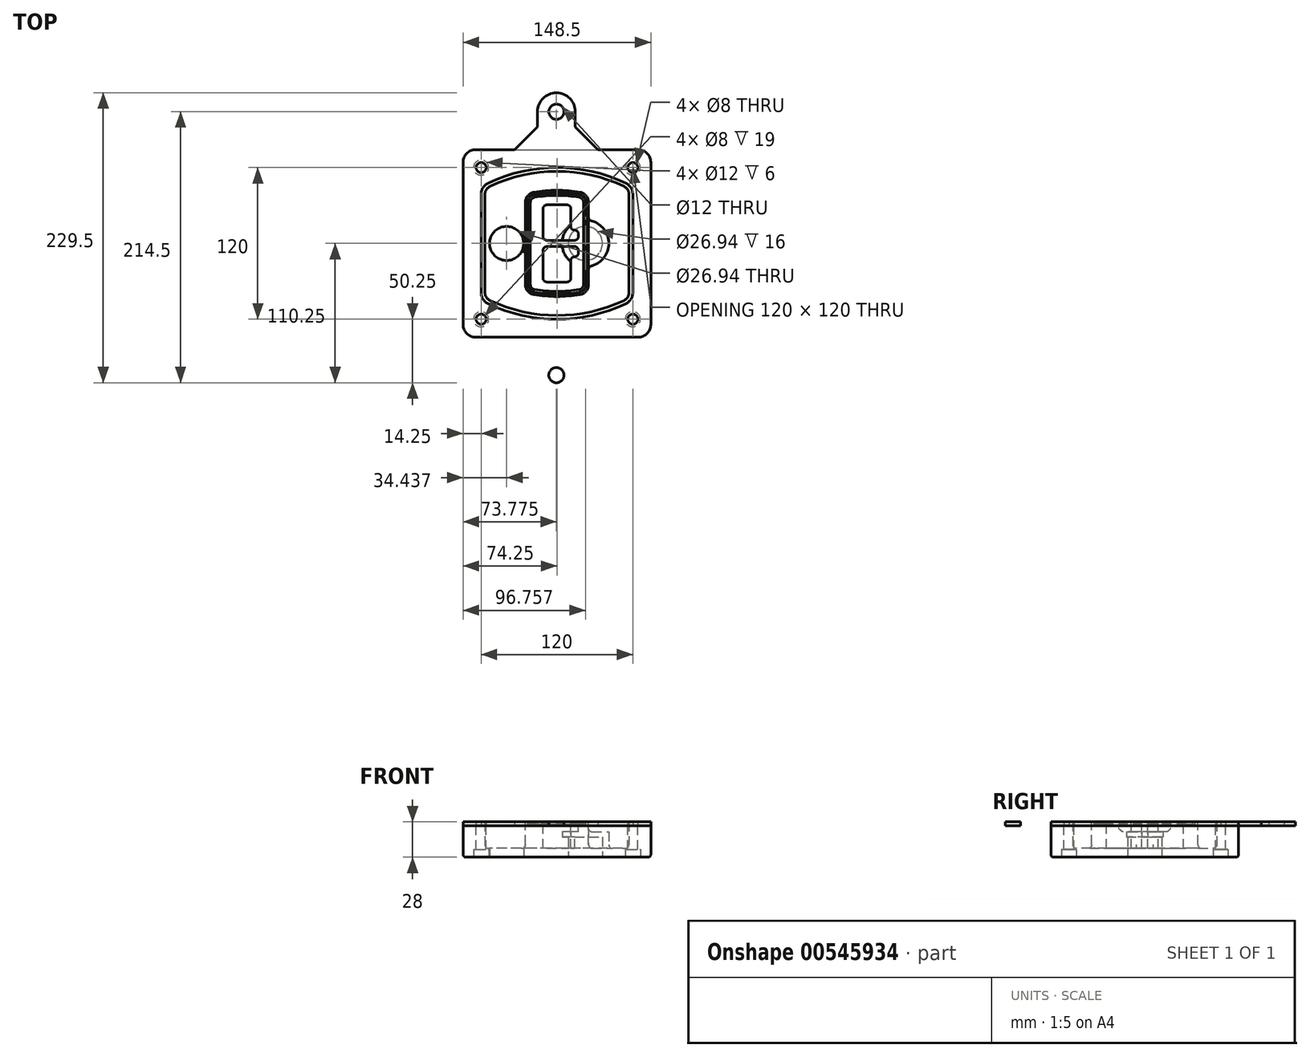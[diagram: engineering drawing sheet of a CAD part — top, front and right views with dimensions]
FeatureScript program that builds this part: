
annotation { "Feature Type Name" : "Feature", "Feature Type Description" : "" }
export const myFeature = defineFeature(function(context is Context, id is Id, definition is map)
    precondition{}
    {
        {
            var Q0;
            Q0=qCreatedBy(makeId("Top.planeOp"),FACE);
            var sketch = newSketch(context, id + "F0", { "sketchPlane" : qUnion([Q0])});
            skPoint(sketch, "E0.rect.middle", {"position": v(0, 0) * mm});
            skLineSegment(sketch, "E1.bottom", {"start": v(-64.25, -74.25) * mm, "end": v(64.25, -74.25) * mm});
            skLineSegment(sketch, "E1.top", {"start": v(-64.25, 74.25) * mm, "end": v(64.25, 74.25) * mm});
            skLineSegment(sketch, "E1.left", {"start": v(-74.25, -64.25) * mm, "end": v(-74.25, 64.25) * mm});
            skLineSegment(sketch, "E1.right", {"start": v(74.25, -64.25) * mm, "end": v(74.25, 64.25) * mm});
            skLineSegment(sketch, "E2", {"start": v(-74.25, 74.25) * mm, "end": v(74.25, -74.25) * mm, "construction": true});
            skLineSegment(sketch, "E3", {"start": v(74.25, 74.25) * mm, "end": v(-74.25, -74.25) * mm, "construction": true});
            skCircle(sketch, "E4", {"center": v(-60, 60) * mm, "radius": 4 * mm});
            skCircle(sketch, "E5", {"center": v(60, 60) * mm, "radius": 4 * mm});
            skCircle(sketch, "E6", {"center": v(60, -60) * mm, "radius": 4 * mm});
            skCircle(sketch, "E7", {"center": v(-60, -60) * mm, "radius": 4 * mm});
            skLineSegment(sketch, "E8", {"start": v(-60, 60) * mm, "end": v(60, 60) * mm, "construction": true});
            skLineSegment(sketch, "E9", {"start": v(60, 60) * mm, "end": v(60, -60) * mm, "construction": true});
            skLineSegment(sketch, "E10", {"start": v(60, -60) * mm, "end": v(-60, -60) * mm, "construction": true});
            skLineSegment(sketch, "E11", {"start": v(-60, -60) * mm, "end": v(-60, 60) * mm, "construction": true});
            skLineSegment(sketch, "E12", {"start": v(-60, 38.83) * mm, "end": v(-60, -38.83) * mm});
            skLineSegment(sketch, "E13", {"start": v(60, 38.83) * mm, "end": v(60, -38.83) * mm});
            skArc(sketch, "E14", {"start": v(54.26, 47.88) * mm, "mid": v(0, 60) * mm, "end": v(-54.26, 47.88) * mm});
            skArc(sketch, "E15", {"start": v(-54.26, -47.88) * mm, "mid": v(0, -60) * mm, "end": v(54.26, -47.88) * mm});
            skLineSegment(sketch, "E16", {"start": v(-60, 0) * mm, "end": v(60, 0) * mm, "construction": true});
            skPoint(sketch, "E17.visualSharp", {"position": v(-60, -45) * mm});
            skArc(sketch, "E17.filletArc", {"start": v(-60, -38.83) * mm, "mid": v(-58.44, -44.2) * mm, "end": v(-54.26, -47.88) * mm});
            skPoint(sketch, "E18.visualSharp", {"position": v(-60, 45) * mm});
            skArc(sketch, "E18.filletArc", {"start": v(-54.26, 47.88) * mm, "mid": v(-58.44, 44.2) * mm, "end": v(-60, 38.83) * mm});
            skPoint(sketch, "E19.visualSharp", {"position": v(60, 45) * mm});
            skArc(sketch, "E19.filletArc", {"start": v(60, 38.83) * mm, "mid": v(58.44, 44.2) * mm, "end": v(54.26, 47.88) * mm});
            skPoint(sketch, "E20.visualSharp", {"position": v(60, -45) * mm});
            skArc(sketch, "E20.filletArc", {"start": v(54.26, -47.88) * mm, "mid": v(58.44, -44.2) * mm, "end": v(60, -38.83) * mm});
            skPoint(sketch, "E21.visualSharp", {"position": v(-74.25, 74.25) * mm});
            skArc(sketch, "E21.filletArc", {"start": v(-64.25, 74.25) * mm, "mid": v(-71.32, 71.32) * mm, "end": v(-74.25, 64.25) * mm});
            skPoint(sketch, "E22.visualSharp", {"position": v(74.25, 74.25) * mm});
            skArc(sketch, "E22.filletArc", {"start": v(74.25, 64.25) * mm, "mid": v(71.32, 71.32) * mm, "end": v(64.25, 74.25) * mm});
            skPoint(sketch, "E23.visualSharp", {"position": v(74.25, -74.25) * mm});
            skArc(sketch, "E23.filletArc", {"start": v(64.25, -74.25) * mm, "mid": v(71.32, -71.32) * mm, "end": v(74.25, -64.25) * mm});
            skPoint(sketch, "E24.visualSharp", {"position": v(-74.25, -74.25) * mm});
            skArc(sketch, "E24.filletArc", {"start": v(-74.25, -64.25) * mm, "mid": v(-71.32, -71.32) * mm, "end": v(-64.25, -74.25) * mm});
            skArc(sketch, "E25.0", {"start": v(57, 38.83) * mm, "mid": v(55.9, 42.58) * mm, "end": v(52.98, 45.17) * mm});
            skLineSegment(sketch, "E25.1", {"start": v(57, 38.83) * mm, "end": v(57, -38.83) * mm});
            skArc(sketch, "E25.2", {"start": v(52.98, -45.17) * mm, "mid": v(55.9, -42.58) * mm, "end": v(57, -38.83) * mm});
            skArc(sketch, "E25.3", {"start": v(-52.98, -45.17) * mm, "mid": v(0, -57) * mm, "end": v(52.98, -45.17) * mm});
            skArc(sketch, "E25.4", {"start": v(-57, -38.83) * mm, "mid": v(-55.9, -42.58) * mm, "end": v(-52.98, -45.17) * mm});
            skArc(sketch, "E25.5", {"start": v(52.98, 45.17) * mm, "mid": v(0, 57) * mm, "end": v(-52.98, 45.17) * mm});
            skLineSegment(sketch, "E25.6", {"start": v(-57, 38.83) * mm, "end": v(-57, -38.83) * mm});
            skArc(sketch, "E25.7", {"start": v(-52.98, 45.17) * mm, "mid": v(-55.9, 42.58) * mm, "end": v(-57, 38.83) * mm});
            skArc(sketch, "E26.0", {"start": v(-55.96, 51.5) * mm, "mid": v(-61.82, 46.33) * mm, "end": v(-64, 38.83) * mm});
            skArc(sketch, "E26.1", {"start": v(55.96, 51.5) * mm, "mid": v(0, 64) * mm, "end": v(-55.96, 51.5) * mm});
            skArc(sketch, "E26.2", {"start": v(64, 38.83) * mm, "mid": v(61.82, 46.33) * mm, "end": v(55.96, 51.5) * mm});
            skLineSegment(sketch, "E26.3", {"start": v(64, 38.83) * mm, "end": v(64, -38.83) * mm});
            skArc(sketch, "E26.4", {"start": v(55.96, -51.5) * mm, "mid": v(61.82, -46.33) * mm, "end": v(64, -38.83) * mm});
            skLineSegment(sketch, "E26.5", {"start": v(-64, 38.83) * mm, "end": v(-64, -38.83) * mm});
            skArc(sketch, "E26.6", {"start": v(-55.96, -51.5) * mm, "mid": v(0, -64) * mm, "end": v(55.96, -51.5) * mm});
            skArc(sketch, "E26.7", {"start": v(-64, -38.83) * mm, "mid": v(-61.82, -46.33) * mm, "end": v(-55.96, -51.5) * mm});
            skSolve(sketch);
        }
        {
            var Q0;
            Q0=makeQuery(id+"F0.imprint","IMPRINT",FACE,{"disambiguationData":[TD([[makeQuery(id+"F0.imprint","IMPRINT",EDGE,{"derivedFrom":sQuery(id+"F0.wireOp",EDGE,"E1.bottom")}),1.0]])]});
            var Q1;
            Q1=makeQuery(id+"F0.imprint","IMPRINT",FACE,{"disambiguationData":[TD([[makeQuery(id+"F0.imprint","IMPRINT",EDGE,{"derivedFrom":sQuery(id+"F0.wireOp",EDGE,"E12")}),1.0]])]});
            var Q2;
            Q2=makeQuery(id+"F0.imprint","IMPRINT",FACE,{"disambiguationData":[TD([[makeQuery(id+"F0.imprint","IMPRINT",EDGE,{"derivedFrom":sQuery(id+"F0.wireOp",EDGE,"E25.0")}),1.0]])]});
            var Q3;
            Q3=makeQuery(id+"F0.imprint","IMPRINT",FACE,{"disambiguationData":[TD([[makeQuery(id+"F0.imprint","IMPRINT",EDGE,{"derivedFrom":sQuery(id+"F0.wireOp",EDGE,"E12")}),-1.0]])]});
            extrude(context, id + "F1", {"entities" : qUnion([Q0, Q1, Q2, Q3]), "oppositeDirection" : true, "depth" : 25 * mm});
        }
        {
            var Q0;
            Q0=makeQuery(id+"F0.imprint","IMPRINT",FACE,{"disambiguationData":[TD([[makeQuery(id+"F0.imprint","IMPRINT",EDGE,{"derivedFrom":sQuery(id+"F0.wireOp",EDGE,"E12")}),1.0]])]});
            extrude(context, id + "F2", {"entities" : qUnion([Q0]), "operationType" : NewBodyOperationType.ADD, "depth" : 3 * mm});
        }
        {
            var Q0;
            Q0=makeQuery(id+"F0.imprint","IMPRINT",FACE,{"disambiguationData":[TD([[makeQuery(id+"F0.imprint","IMPRINT",EDGE,{"derivedFrom":sQuery(id+"F0.wireOp",EDGE,"E25.0")}),1.0]])]});
            extrude(context, id + "F3", {"entities" : qUnion([Q0]), "operationType" : NewBodyOperationType.REMOVE, "oppositeDirection" : true, "depth" : 18 * mm});
        }
        {
            var Q0;
            Q0=makeQuery(id+"F2.opExtrude","CAP_FACE",FACE,{"disambiguationData":[OSD([sQuery(id+"F0.wireOp",EDGE,"E12"),sQuery(id+"F0.wireOp",EDGE,"E13"),sQuery(id+"F0.wireOp",EDGE,"E14"),sQuery(id+"F0.wireOp",EDGE,"E15"),sQuery(id+"F0.wireOp",EDGE,"E17.filletArc"),sQuery(id+"F0.wireOp",EDGE,"E18.filletArc"),sQuery(id+"F0.wireOp",EDGE,"E19.filletArc"),sQuery(id+"F0.wireOp",EDGE,"E20.filletArc"),sQuery(id+"F0.wireOp",EDGE,"E25.0"),sQuery(id+"F0.wireOp",EDGE,"E25.1"),sQuery(id+"F0.wireOp",EDGE,"E25.2"),sQuery(id+"F0.wireOp",EDGE,"E25.3"),sQuery(id+"F0.wireOp",EDGE,"E25.4"),sQuery(id+"F0.wireOp",EDGE,"E25.5"),sQuery(id+"F0.wireOp",EDGE,"E25.6"),sQuery(id+"F0.wireOp",EDGE,"E25.7")])],"isStart":false});
            var sketch = newSketch(context, id + "F4", { "sketchPlane" : qUnion([Q0])});
            skArc(sketch, "E27.0", {"start": v(-18.34, -40.45) * mm, "mid": v(0, -42) * mm, "end": v(18.34, -40.45) * mm});
            skArc(sketch, "E28.0", {"start": v(18.34, 40.45) * mm, "mid": v(0, 42) * mm, "end": v(-18.34, 40.45) * mm});
            skLineSegment(sketch, "E29", {"start": v(-25, 32.57) * mm, "end": v(-25, -32.57) * mm});
            skLineSegment(sketch, "E30", {"start": v(25, 32.57) * mm, "end": v(25, -32.57) * mm});
            skLineSegment(sketch, "E31", {"start": v(-25, 39.1) * mm, "end": v(25, 39.1) * mm, "construction": true});
            skLineSegment(sketch, "E32", {"start": v(-25, -39.1) * mm, "end": v(25, -39.1) * mm, "construction": true});
            skPoint(sketch, "E33.visualSharp", {"position": v(-25, 39.1) * mm});
            skArc(sketch, "E33.filletArc", {"start": v(-18.34, 40.45) * mm, "mid": v(-23.11, 37.73) * mm, "end": v(-25, 32.57) * mm});
            skPoint(sketch, "E34.visualSharp", {"position": v(25, 39.1) * mm});
            skArc(sketch, "E34.filletArc", {"start": v(25, 32.57) * mm, "mid": v(23.11, 37.73) * mm, "end": v(18.34, 40.45) * mm});
            skPoint(sketch, "E35.visualSharp", {"position": v(25, -39.1) * mm});
            skArc(sketch, "E35.filletArc", {"start": v(18.34, -40.45) * mm, "mid": v(23.11, -37.73) * mm, "end": v(25, -32.57) * mm});
            skPoint(sketch, "E36.visualSharp", {"position": v(-25, -39.1) * mm});
            skArc(sketch, "E36.filletArc", {"start": v(-25, -32.57) * mm, "mid": v(-23.11, -37.73) * mm, "end": v(-18.34, -40.45) * mm});
            skArc(sketch, "E37.0", {"start": v(52.98, 45.17) * mm, "mid": v(0, 57) * mm, "end": v(-52.98, 45.17) * mm});
            skArc(sketch, "E37.1", {"start": v(-52.98, 45.17) * mm, "mid": v(-55.9, 42.58) * mm, "end": v(-57, 38.83) * mm});
            skLineSegment(sketch, "E37.2", {"start": v(-57, 38.83) * mm, "end": v(-57, -38.83) * mm});
            skArc(sketch, "E37.3", {"start": v(-57, -38.83) * mm, "mid": v(-55.9, -42.58) * mm, "end": v(-52.98, -45.17) * mm});
            skArc(sketch, "E37.4", {"start": v(-52.98, -45.17) * mm, "mid": v(0, -57) * mm, "end": v(52.98, -45.17) * mm});
            skArc(sketch, "E37.5", {"start": v(52.98, -45.17) * mm, "mid": v(55.9, -42.58) * mm, "end": v(57, -38.83) * mm});
            skLineSegment(sketch, "E37.6", {"start": v(57, 38.83) * mm, "end": v(57, -38.83) * mm});
            skArc(sketch, "E37.7", {"start": v(57, 38.83) * mm, "mid": v(55.9, 42.58) * mm, "end": v(52.98, 45.17) * mm});
            skLineSegment(sketch, "E38.0", {"start": v(23, 32.57) * mm, "end": v(23, -32.57) * mm});
            skArc(sketch, "E38.1", {"start": v(18, -38.48) * mm, "mid": v(21.58, -36.44) * mm, "end": v(23, -32.57) * mm});
            skArc(sketch, "E38.2", {"start": v(-18, -38.48) * mm, "mid": v(0, -40) * mm, "end": v(18, -38.48) * mm});
            skArc(sketch, "E38.3", {"start": v(-23, -32.57) * mm, "mid": v(-21.58, -36.44) * mm, "end": v(-18, -38.48) * mm});
            skLineSegment(sketch, "E38.4", {"start": v(-23, 32.57) * mm, "end": v(-23, -32.57) * mm});
            skArc(sketch, "E38.5", {"start": v(23, 32.57) * mm, "mid": v(21.58, 36.44) * mm, "end": v(18, 38.48) * mm});
            skArc(sketch, "E38.6", {"start": v(-18, 38.48) * mm, "mid": v(-21.58, 36.44) * mm, "end": v(-23, 32.57) * mm});
            skArc(sketch, "E38.7", {"start": v(18, 38.48) * mm, "mid": v(0, 40) * mm, "end": v(-18, 38.48) * mm});
            skArc(sketch, "E39.0", {"start": v(21, 32.57) * mm, "mid": v(20.06, 35.15) * mm, "end": v(17.67, 36.5) * mm});
            skLineSegment(sketch, "E39.1", {"start": v(21, 32.57) * mm, "end": v(21, -32.57) * mm});
            skArc(sketch, "E39.2", {"start": v(17.67, -36.5) * mm, "mid": v(20.06, -35.15) * mm, "end": v(21, -32.57) * mm});
            skArc(sketch, "E39.3", {"start": v(-17.67, -36.5) * mm, "mid": v(0, -38) * mm, "end": v(17.67, -36.5) * mm});
            skArc(sketch, "E39.4", {"start": v(-21, -32.57) * mm, "mid": v(-20.06, -35.15) * mm, "end": v(-17.67, -36.5) * mm});
            skArc(sketch, "E39.5", {"start": v(17.67, 36.5) * mm, "mid": v(0, 38) * mm, "end": v(-17.67, 36.5) * mm});
            skLineSegment(sketch, "E39.6", {"start": v(-21, 32.57) * mm, "end": v(-21, -32.57) * mm});
            skArc(sketch, "E39.7", {"start": v(-17.67, 36.5) * mm, "mid": v(-20.06, 35.15) * mm, "end": v(-21, 32.57) * mm});
            skLineSegment(sketch, "E40", {"start": v(-25, 0) * mm, "end": v(25, 0) * mm, "construction": true});
            skLineSegment(sketch, "E41", {"start": v(-11, 5.5) * mm, "end": v(-11, 27.5) * mm});
            skLineSegment(sketch, "E42", {"start": v(-8, 30.5) * mm, "end": v(8, 30.5) * mm});
            skLineSegment(sketch, "E43", {"start": v(11, 27.5) * mm, "end": v(11, 13.5) * mm});
            skLineSegment(sketch, "E44", {"start": v(14, 10.5) * mm, "end": v(14, 10.5) * mm});
            skLineSegment(sketch, "E45", {"start": v(17, 7.5) * mm, "end": v(17, 5.5) * mm});
            skLineSegment(sketch, "E46", {"start": v(14, 2.5) * mm, "end": v(-8, 2.5) * mm});
            skPoint(sketch, "E47.visualSharp", {"position": v(-11, 30.5) * mm});
            skArc(sketch, "E47.filletArc", {"start": v(-8, 30.5) * mm, "mid": v(-10.12, 29.62) * mm, "end": v(-11, 27.5) * mm});
            skPoint(sketch, "E48.visualSharp", {"position": v(11, 30.5) * mm});
            skArc(sketch, "E48.filletArc", {"start": v(11, 27.5) * mm, "mid": v(10.12, 29.62) * mm, "end": v(8, 30.5) * mm});
            skPoint(sketch, "E49.visualSharp", {"position": v(11, 10.5) * mm});
            skArc(sketch, "E49.filletArc", {"start": v(11, 13.5) * mm, "mid": v(11.88, 11.38) * mm, "end": v(14, 10.5) * mm});
            skPoint(sketch, "E50.visualSharp", {"position": v(17, 10.5) * mm});
            skArc(sketch, "E50.filletArc", {"start": v(17, 7.5) * mm, "mid": v(16.12, 9.62) * mm, "end": v(14, 10.5) * mm});
            skPoint(sketch, "E51.visualSharp", {"position": v(17, 2.5) * mm});
            skArc(sketch, "E51.filletArc", {"start": v(14, 2.5) * mm, "mid": v(16.12, 3.38) * mm, "end": v(17, 5.5) * mm});
            skPoint(sketch, "E52.visualSharp", {"position": v(-11, 2.5) * mm});
            skArc(sketch, "E52.filletArc", {"start": v(-11, 5.5) * mm, "mid": v(-10.12, 3.38) * mm, "end": v(-8, 2.5) * mm});
            skLineSegment(sketch, "E53.0.MirrorCS", {"start": v(14, -2.5) * mm, "end": v(-8, -2.5) * mm});
            skArc(sketch, "E54.0.MirrorCS", {"start": v(-11, -5.5) * mm, "mid": v(-10.12, -3.38) * mm, "end": v(-8, -2.5) * mm});
            skLineSegment(sketch, "E55.0.MirrorCS", {"start": v(-11, -5.5) * mm, "end": v(-11, -27.5) * mm});
            skArc(sketch, "E56.0.MirrorCS", {"start": v(-8, -30.5) * mm, "mid": v(-10.12, -29.62) * mm, "end": v(-11, -27.5) * mm});
            skLineSegment(sketch, "E57.0.MirrorCS", {"start": v(-8, -30.5) * mm, "end": v(8, -30.5) * mm});
            skArc(sketch, "E58.0.MirrorCS", {"start": v(11, -27.5) * mm, "mid": v(10.12, -29.62) * mm, "end": v(8, -30.5) * mm});
            skLineSegment(sketch, "E59.0.MirrorCS", {"start": v(11, -27.5) * mm, "end": v(11, -13.5) * mm});
            skArc(sketch, "E60.0.MirrorCS", {"start": v(11, -13.5) * mm, "mid": v(11.88, -11.38) * mm, "end": v(14, -10.5) * mm});
            skArc(sketch, "E61.0.MirrorCS", {"start": v(17, -7.5) * mm, "mid": v(16.12, -9.62) * mm, "end": v(14, -10.5) * mm});
            skLineSegment(sketch, "E62.0.MirrorCS", {"start": v(17, -7.5) * mm, "end": v(17, -5.5) * mm});
            skArc(sketch, "E63.0.MirrorCS", {"start": v(14, -2.5) * mm, "mid": v(16.12, -3.38) * mm, "end": v(17, -5.5) * mm});
            skSolve(sketch);
        }
        {
            var Q0;
            Q0=makeQuery(id+"F4.imprint","IMPRINT",FACE,{"disambiguationData":[TD([[makeQuery(id+"F4.imprint","IMPRINT",EDGE,{"derivedFrom":sQuery(id+"F4.wireOp",EDGE,"E27.0")}),1.0]])]});
            var Q1;
            Q1=makeQuery(id+"F4.imprint","IMPRINT",FACE,{"disambiguationData":[TD([[makeQuery(id+"F4.imprint","IMPRINT",EDGE,{"derivedFrom":sQuery(id+"F4.wireOp",EDGE,"E38.0")}),-1.0]])]});
            var Q2;
            Q2=makeQuery(id+"F4.imprint","IMPRINT",FACE,{"disambiguationData":[TD([[makeQuery(id+"F4.imprint","IMPRINT",EDGE,{"derivedFrom":sQuery(id+"F4.wireOp",EDGE,"E39.0")}),1.0]])]});
            extrude(context, id + "F5", {"entities" : qUnion([Q0, Q1, Q2]), "operationType" : NewBodyOperationType.ADD, "endBound" : BoundingType.UP_TO_NEXT, "oppositeDirection" : true, "depth" : 25 * mm});
        }
        {
            var Q0;
            Q0=makeQuery(id+"F4.imprint","IMPRINT",FACE,{"disambiguationData":[TD([[makeQuery(id+"F4.imprint","IMPRINT",EDGE,{"derivedFrom":sQuery(id+"F4.wireOp",EDGE,"E38.0")}),-1.0]])]});
            extrude(context, id + "F6", {"entities" : qUnion([Q0]), "operationType" : NewBodyOperationType.REMOVE, "oppositeDirection" : true, "depth" : 2 * mm});
        }
        {
            var Q0;
            Q0=makeQuery(id+"F1.opExtrude","CAP_FACE",FACE,{"disambiguationData":[OSD([sQuery(id+"F0.wireOp",EDGE,"E1.bottom"),sQuery(id+"F0.wireOp",EDGE,"E1.top"),sQuery(id+"F0.wireOp",EDGE,"E1.left"),sQuery(id+"F0.wireOp",EDGE,"E1.right"),sQuery(id+"F0.wireOp",EDGE,"E4"),sQuery(id+"F0.wireOp",EDGE,"E5"),sQuery(id+"F0.wireOp",EDGE,"E6"),sQuery(id+"F0.wireOp",EDGE,"E7"),sQuery(id+"F0.wireOp",EDGE,"E21.filletArc"),sQuery(id+"F0.wireOp",EDGE,"E22.filletArc"),sQuery(id+"F0.wireOp",EDGE,"E23.filletArc"),sQuery(id+"F0.wireOp",EDGE,"E24.filletArc")])],"isStart":false});
            var sketch = newSketch(context, id + "F7", { "sketchPlane" : qUnion([Q0])});
            skCircle(sketch, "E64", {"center": v(22.5, 0) * mm, "radius": 13.47 * mm});
            skCircle(sketch, "E65", {"center": v(-39.81, 0) * mm, "radius": 13.47 * mm});
            skLineSegment(sketch, "E66", {"start": v(74.25, 0) * mm, "end": v(-74.25, 0) * mm});
            skCircle(sketch, "E67", {"center": v(22.5, 0) * mm, "radius": 18.47 * mm});
            skCircle(sketch, "E68", {"center": v(60, -60) * mm, "radius": 6 * mm});
            skCircle(sketch, "E69", {"center": v(-60, -60) * mm, "radius": 6 * mm});
            skCircle(sketch, "E70", {"center": v(-60, 60) * mm, "radius": 6 * mm});
            skCircle(sketch, "E71", {"center": v(60, 60) * mm, "radius": 6 * mm});
            skSolve(sketch);
        }
        {
            var Q0;
            {var subQ1=sQuery(id+"F7.wireOp",EDGE,"E66");var subQ4=sQuery(id+"F7.wireOp",EDGE,"E64");var subQ6=makeQuery(id+"F7.imprint","INTERSECT",VERTEX,{"disambiguationData":[OD(0.0)],"derivedFrom":[subQ4,subQ1]});Q0=makeQuery(id+"F7.imprint","IMPRINT",FACE,{"disambiguationData":[TD([[makeQuery(id+"F7.imprint","IMPRINT",EDGE,{"disambiguationData":[TD([[subQ6,-1.0]])],"derivedFrom":subQ4}),-1.0]])]});}
            var Q1;
            {var subQ0=sQuery(id+"F7.wireOp",EDGE,"E66");var subQ1=sQuery(id+"F7.wireOp",EDGE,"E64");var subQ3=makeQuery(id+"F7.imprint","INTERSECT",VERTEX,{"disambiguationData":[OD(0.0)],"derivedFrom":[subQ1,subQ0]});Q1=makeQuery(id+"F7.imprint","IMPRINT",FACE,{"disambiguationData":[TD([[makeQuery(id+"F7.imprint","IMPRINT",EDGE,{"disambiguationData":[TD([[subQ3,-1.0]])],"derivedFrom":subQ1}),1.0]])]});}
            var Q2;
            {var subQ0=sQuery(id+"F7.wireOp",EDGE,"E66");var subQ1=sQuery(id+"F7.wireOp",EDGE,"E64");var subQ3=makeQuery(id+"F7.imprint","INTERSECT",VERTEX,{"disambiguationData":[OD(0.0)],"derivedFrom":[subQ1,subQ0]});Q2=makeQuery(id+"F7.imprint","IMPRINT",FACE,{"disambiguationData":[TD([[makeQuery(id+"F7.imprint","IMPRINT",EDGE,{"disambiguationData":[TD([[subQ3,1.0]])],"derivedFrom":subQ1}),1.0]])]});}
            var Q3;
            {var subQ1=sQuery(id+"F7.wireOp",EDGE,"E66");var subQ4=sQuery(id+"F7.wireOp",EDGE,"E64");var subQ6=makeQuery(id+"F7.imprint","INTERSECT",VERTEX,{"disambiguationData":[OD(0.0)],"derivedFrom":[subQ4,subQ1]});Q3=makeQuery(id+"F7.imprint","IMPRINT",FACE,{"disambiguationData":[TD([[makeQuery(id+"F7.imprint","IMPRINT",EDGE,{"disambiguationData":[TD([[subQ6,1.0]])],"derivedFrom":subQ4}),-1.0]])]});}
            extrude(context, id + "F8", {"entities" : qUnion([Q0, Q1, Q2, Q3]), "operationType" : NewBodyOperationType.ADD, "oppositeDirection" : true, "depth" : 20 * mm});
        }
        {
            var Q0;
            {var subQ0=sQuery(id+"F7.wireOp",EDGE,"E66");var subQ1=sQuery(id+"F7.wireOp",EDGE,"E64");var subQ3=makeQuery(id+"F7.imprint","INTERSECT",VERTEX,{"disambiguationData":[OD(0.0)],"derivedFrom":[subQ1,subQ0]});Q0=makeQuery(id+"F7.imprint","IMPRINT",FACE,{"disambiguationData":[TD([[makeQuery(id+"F7.imprint","IMPRINT",EDGE,{"disambiguationData":[TD([[subQ3,-1.0]])],"derivedFrom":subQ1}),1.0]])]});}
            var Q1;
            {var subQ0=sQuery(id+"F7.wireOp",EDGE,"E66");var subQ1=sQuery(id+"F7.wireOp",EDGE,"E64");var subQ3=makeQuery(id+"F7.imprint","INTERSECT",VERTEX,{"disambiguationData":[OD(0.0)],"derivedFrom":[subQ1,subQ0]});Q1=makeQuery(id+"F7.imprint","IMPRINT",FACE,{"disambiguationData":[TD([[makeQuery(id+"F7.imprint","IMPRINT",EDGE,{"disambiguationData":[TD([[subQ3,1.0]])],"derivedFrom":subQ1}),1.0]])]});}
            extrude(context, id + "F9", {"entities" : qUnion([Q0, Q1]), "operationType" : NewBodyOperationType.REMOVE, "oppositeDirection" : true, "depth" : 16 * mm});
        }
        {
            var Q0;
            {var subQ0=sQuery(id+"F7.wireOp",EDGE,"E66");var subQ1=sQuery(id+"F7.wireOp",EDGE,"E65");var subQ3=makeQuery(id+"F7.imprint","INTERSECT",VERTEX,{"disambiguationData":[OD(0.0)],"derivedFrom":[subQ1,subQ0]});Q0=makeQuery(id+"F7.imprint","IMPRINT",FACE,{"disambiguationData":[TD([[makeQuery(id+"F7.imprint","IMPRINT",EDGE,{"disambiguationData":[TD([[subQ3,-1.0]])],"derivedFrom":subQ1}),1.0]])]});}
            var Q1;
            {var subQ0=sQuery(id+"F7.wireOp",EDGE,"E66");var subQ1=sQuery(id+"F7.wireOp",EDGE,"E65");var subQ3=makeQuery(id+"F7.imprint","INTERSECT",VERTEX,{"disambiguationData":[OD(0.0)],"derivedFrom":[subQ1,subQ0]});Q1=makeQuery(id+"F7.imprint","IMPRINT",FACE,{"disambiguationData":[TD([[makeQuery(id+"F7.imprint","IMPRINT",EDGE,{"disambiguationData":[TD([[subQ3,1.0]])],"derivedFrom":subQ1}),1.0]])]});}
            extrude(context, id + "F10", {"entities" : qUnion([Q0, Q1]), "operationType" : NewBodyOperationType.REMOVE, "oppositeDirection" : true, "depth" : 25 * mm});
        }
        {
            var Q0;
            Q0=makeQuery(id+"F7.imprint","IMPRINT",FACE,{"disambiguationData":[TD([[makeQuery(id+"F7.imprint","IMPRINT",EDGE,{"derivedFrom":sQuery(id+"F7.wireOp",EDGE,"E68")}),1.0]])]});
            var Q1;
            Q1=makeQuery(id+"F7.imprint","IMPRINT",FACE,{"disambiguationData":[TD([[makeQuery(id+"F7.imprint","IMPRINT",EDGE,{"derivedFrom":makeQuery(id+"F1.opExtrude","CAP_EDGE",EDGE,{"disambiguationData":[OSD([sQuery(id+"F0.wireOp",EDGE,"E5")])],"isStart":false})}),-1.0]])]});
            var Q2;
            Q2=makeQuery(id+"F7.imprint","IMPRINT",FACE,{"disambiguationData":[TD([[makeQuery(id+"F7.imprint","IMPRINT",EDGE,{"derivedFrom":sQuery(id+"F7.wireOp",EDGE,"E69")}),1.0]])]});
            var Q3;
            Q3=makeQuery(id+"F7.imprint","IMPRINT",FACE,{"disambiguationData":[TD([[makeQuery(id+"F7.imprint","IMPRINT",EDGE,{"derivedFrom":makeQuery(id+"F1.opExtrude","CAP_EDGE",EDGE,{"disambiguationData":[OSD([sQuery(id+"F0.wireOp",EDGE,"E4")])],"isStart":false})}),-1.0]])]});
            var Q4;
            Q4=makeQuery(id+"F7.imprint","IMPRINT",FACE,{"disambiguationData":[TD([[makeQuery(id+"F7.imprint","IMPRINT",EDGE,{"derivedFrom":sQuery(id+"F7.wireOp",EDGE,"E70")}),1.0]])]});
            var Q5;
            Q5=makeQuery(id+"F7.imprint","IMPRINT",FACE,{"disambiguationData":[TD([[makeQuery(id+"F7.imprint","IMPRINT",EDGE,{"derivedFrom":makeQuery(id+"F1.opExtrude","CAP_EDGE",EDGE,{"disambiguationData":[OSD([sQuery(id+"F0.wireOp",EDGE,"E7")])],"isStart":false})}),-1.0]])]});
            var Q6;
            Q6=makeQuery(id+"F7.imprint","IMPRINT",FACE,{"disambiguationData":[TD([[makeQuery(id+"F7.imprint","IMPRINT",EDGE,{"derivedFrom":sQuery(id+"F7.wireOp",EDGE,"E71")}),1.0]])]});
            var Q7;
            Q7=makeQuery(id+"F7.imprint","IMPRINT",FACE,{"disambiguationData":[TD([[makeQuery(id+"F7.imprint","IMPRINT",EDGE,{"derivedFrom":makeQuery(id+"F1.opExtrude","CAP_EDGE",EDGE,{"disambiguationData":[OSD([sQuery(id+"F0.wireOp",EDGE,"E6")])],"isStart":false})}),-1.0]])]});
            extrude(context, id + "F11", {"entities" : qUnion([Q0, Q1, Q2, Q3, Q4, Q5, Q6, Q7]), "operationType" : NewBodyOperationType.REMOVE, "oppositeDirection" : true, "depth" : 6 * mm});
        }
        {
            var Q0;
            Q0=makeQuery(id+"F9.boolean.opBoolean","COPY",FACE,{"derivedFrom":makeQuery(id+"F9.opExtrude","CAP_FACE",FACE,{"disambiguationData":[OSD([sQuery(id+"F7.wireOp",EDGE,"E64")])],"isStart":false})});
            var sketch = newSketch(context, id + "F12", { "sketchPlane" : qUnion([Q0])});
            skArc(sketch, "E72.0", {"start": v(11, 14.45) * mm, "mid": v(6.45, 9.13) * mm, "end": v(4.2, 2.5) * mm});
            skArc(sketch, "E72.1", {"start": v(4.2, -2.5) * mm, "mid": v(6.45, -9.13) * mm, "end": v(11, -14.45) * mm});
            skLineSegment(sketch, "E73", {"start": v(4.2, -2.5) * mm, "end": v(14, -2.5) * mm});
            skLineSegment(sketch, "E74.0", {"start": v(14, 2.5) * mm, "end": v(4.2, 2.5) * mm});
            skArc(sketch, "E74.1", {"start": v(14, 2.5) * mm, "mid": v(16.12, 3.38) * mm, "end": v(17, 5.5) * mm});
            skLineSegment(sketch, "E74.2", {"start": v(17, 7.5) * mm, "end": v(17, 5.5) * mm});
            skArc(sketch, "E74.3", {"start": v(17, 7.5) * mm, "mid": v(16.12, 9.62) * mm, "end": v(14, 10.5) * mm});
            skArc(sketch, "E74.4", {"start": v(11, 13.5) * mm, "mid": v(11.88, 11.38) * mm, "end": v(14, 10.5) * mm});
            skLineSegment(sketch, "E74.5", {"start": v(11, 14.45) * mm, "end": v(11, 13.5) * mm});
            skLineSegment(sketch, "E74.7", {"start": v(14, -2.5) * mm, "end": v(4.2, -2.5) * mm});
            skArc(sketch, "E74.8", {"start": v(14, -2.5) * mm, "mid": v(16.12, -3.38) * mm, "end": v(17, -5.5) * mm});
            skLineSegment(sketch, "E74.9", {"start": v(17, -7.5) * mm, "end": v(17, -5.5) * mm});
            skArc(sketch, "E74.10", {"start": v(17, -7.5) * mm, "mid": v(16.12, -9.62) * mm, "end": v(14, -10.5) * mm});
            skArc(sketch, "E74.11", {"start": v(11, -13.5) * mm, "mid": v(11.88, -11.38) * mm, "end": v(14, -10.5) * mm});
            skLineSegment(sketch, "E74.12", {"start": v(11, -14.45) * mm, "end": v(11, -13.5) * mm});
            skPoint(sketch, "E75.orphan", {"position": v(11, -27.5) * mm});
            skPoint(sketch, "E76.orphan", {"position": v(-8, -2.5) * mm});
            skPoint(sketch, "E77.orphan", {"position": v(-8, 2.5) * mm});
            skPoint(sketch, "E78.orphan", {"position": v(11, 27.5) * mm});
            skSolve(sketch);
        }
        {
            var Q0;
            {var subQ7=sQuery(id+"F12.wireOp",EDGE,"E72.0");var subQ14=sQuery(id+"F12.wireOp",EDGE,"E72.1");var subQ16=sQuery(id+"F12.wireOp",EDGE,"E74.1");var subQ18=sQuery(id+"F12.wireOp",EDGE,"E74.8");Q0=qUnion([makeQuery(id+"F12.imprint","IMPRINT",FACE,{"disambiguationData":[TD([[makeQuery(id+"F12.imprint","IMPRINT",EDGE,{"derivedFrom":subQ7}),1.0]])]}),makeQuery(id+"F12.imprint","IMPRINT",FACE,{"disambiguationData":[TD([[makeQuery(id+"F12.imprint","IMPRINT",EDGE,{"derivedFrom":subQ14}),1.0]])]}),makeQuery(id+"F12.imprint","IMPRINT",FACE,{"disambiguationData":[TD([[makeQuery(id+"F12.imprint","IMPRINT",EDGE,{"derivedFrom":subQ16}),1.0]])]}),makeQuery(id+"F12.imprint","IMPRINT",FACE,{"disambiguationData":[TD([[makeQuery(id+"F12.imprint","IMPRINT",EDGE,{"derivedFrom":subQ18}),-1.0]])]})]);}
            var Q1;
            Q1=makeQuery(id+"F5.boolean.opBoolean","SPLIT",FACE,{"disambiguationData":[TD([makeQuery(id+"F5.opExtrude","SWEPT_FACE",FACE,{"disambiguationData":[OSD([sQuery(id+"F4.wireOp",EDGE,"E41")])]})])],"derivedFrom":makeQuery(id+"F3.boolean.opBoolean","COPY",FACE,{"derivedFrom":makeQuery(id+"F3.opExtrude","CAP_FACE",FACE,{"disambiguationData":[OSD([sQuery(id+"F0.wireOp",EDGE,"E25.0"),sQuery(id+"F0.wireOp",EDGE,"E25.1"),sQuery(id+"F0.wireOp",EDGE,"E25.2"),sQuery(id+"F0.wireOp",EDGE,"E25.3"),sQuery(id+"F0.wireOp",EDGE,"E25.4"),sQuery(id+"F0.wireOp",EDGE,"E25.5"),sQuery(id+"F0.wireOp",EDGE,"E25.6"),sQuery(id+"F0.wireOp",EDGE,"E25.7")])],"isStart":false})})});
            extrude(context, id + "F13", {"entities" : qUnion([Q0]), "operationType" : NewBodyOperationType.REMOVE, "endBound" : BoundingType.UP_TO_SURFACE, "endBoundEntityFace" : qUnion([Q1]), "depth" : 25 * mm});
        }
        {
            var Q0;
            Q0=makeQuery(id+"F3.boolean.opBoolean","COPY",EDGE,{"derivedFrom":makeQuery(id+"F3.opExtrude","CAP_EDGE",EDGE,{"disambiguationData":[OSD([sQuery(id+"F0.wireOp",EDGE,"E25.6")])],"isStart":false})});
            var Q1;
            Q1=makeQuery(id+"F8.boolean.opBoolean","INTERSECT",EDGE,{"derivedFrom":[makeQuery(id+"F5.opExtrude","SWEPT_FACE",FACE,{"disambiguationData":[OSD([sQuery(id+"F4.wireOp",EDGE,"E30")])]}),makeQuery(id+"F8.opExtrude","CAP_FACE",FACE,{"disambiguationData":[OSD([sQuery(id+"F7.wireOp",EDGE,"E67")])],"isStart":false})]});
            var Q2;
            Q2=makeQuery(id+"F8.boolean.opBoolean","INTERSECT",EDGE,{"disambiguationData":[OD(1.0)],"derivedFrom":[makeQuery(id+"F5.opExtrude","SWEPT_FACE",FACE,{"disambiguationData":[OSD([sQuery(id+"F4.wireOp",EDGE,"E30")])]}),makeQuery(id+"F8.opExtrude","SWEPT_FACE",FACE,{"disambiguationData":[OSD([sQuery(id+"F7.wireOp",EDGE,"E67")])]})]});
            var Q3;
            {var subQ0=sQuery(id+"F4.wireOp",EDGE,"E30");Q3=makeQuery(id+"F8.boolean.opBoolean","SPLIT",EDGE,{"disambiguationData":[TD([makeQuery(id+"F5.opExtrude","SWEPT_FACE",FACE,{"disambiguationData":[OSD([sQuery(id+"F4.wireOp",EDGE,"E35.filletArc")])]})])],"derivedFrom":makeQuery(id+"F5.opExtrude","CAP_EDGE",EDGE,{"disambiguationData":[OSD([subQ0])],"isStart":false})});}
            var Q4;
            {var subQ0=sQuery(id+"F0.wireOp",EDGE,"E25.7");var subQ1=sQuery(id+"F0.wireOp",EDGE,"E25.1");var subQ2=sQuery(id+"F0.wireOp",EDGE,"E25.6");var subQ3=sQuery(id+"F0.wireOp",EDGE,"E25.5");var subQ4=sQuery(id+"F0.wireOp",EDGE,"E25.4");var subQ5=sQuery(id+"F0.wireOp",EDGE,"E25.0");var subQ6=sQuery(id+"F0.wireOp",EDGE,"E25.2");var subQ7=sQuery(id+"F0.wireOp",EDGE,"E25.3");Q4=makeQuery(id+"F8.boolean.opBoolean","INTERSECT",EDGE,{"derivedFrom":[makeQuery(id+"F5.boolean.opBoolean","SPLIT",FACE,{"disambiguationData":[TD([makeQuery(id+"F2.opExtrude","SWEPT_FACE",FACE,{"disambiguationData":[OSD([subQ5])]})])],"derivedFrom":makeQuery(id+"F3.boolean.opBoolean","COPY",FACE,{"derivedFrom":makeQuery(id+"F3.opExtrude","CAP_FACE",FACE,{"disambiguationData":[OSD([subQ5,subQ1,subQ6,subQ7,subQ4,subQ3,subQ2,subQ0])],"isStart":false})})}),makeQuery(id+"F8.opExtrude","SWEPT_FACE",FACE,{"disambiguationData":[OSD([sQuery(id+"F7.wireOp",EDGE,"E67")])]})]});}
            var Q5;
            Q5=makeQuery(id+"F8.boolean.opBoolean","INTERSECT",EDGE,{"disambiguationData":[OD(0.0)],"derivedFrom":[makeQuery(id+"F5.opExtrude","SWEPT_FACE",FACE,{"disambiguationData":[OSD([sQuery(id+"F4.wireOp",EDGE,"E30")])]}),makeQuery(id+"F8.opExtrude","SWEPT_FACE",FACE,{"disambiguationData":[OSD([sQuery(id+"F7.wireOp",EDGE,"E67")])]})]});
            fillet(context, id + "F14", {"entities" : qUnion([Q0, Q1, Q2, Q3, Q4, Q5]), "radius" : 3 * mm, "tangentPropagation" : true, "allowEdgeOverflow" : false});
        }
        {
            var Q0;
            Q0=makeQuery(id+"F1.opExtrude","CAP_EDGE",EDGE,{"disambiguationData":[OSD([sQuery(id+"F0.wireOp",EDGE,"E1.bottom")])],"isStart":false});
            fillet(context, id + "F15", {"entities" : qUnion([Q0]), "radius" : 2 * mm, "tangentPropagation" : true, "allowEdgeOverflow" : false});
        }
        {
            var Q0;
            {var subQ0=sQuery(id+"F0.wireOp",EDGE,"E21.filletArc");var subQ1=sQuery(id+"F0.wireOp",EDGE,"E7");var subQ2=sQuery(id+"F0.wireOp",EDGE,"E6");var subQ3=sQuery(id+"F0.wireOp",EDGE,"E5");var subQ4=sQuery(id+"F0.wireOp",EDGE,"E4");var subQ5=sQuery(id+"F0.wireOp",EDGE,"E22.filletArc");var subQ6=sQuery(id+"F0.wireOp",EDGE,"E1.bottom");var subQ7=sQuery(id+"F0.wireOp",EDGE,"E1.right");var subQ8=sQuery(id+"F0.wireOp",EDGE,"E1.top");var subQ9=sQuery(id+"F0.wireOp",EDGE,"E1.left");var subQ10=sQuery(id+"F0.wireOp",EDGE,"E23.filletArc");var subQ11=sQuery(id+"F0.wireOp",EDGE,"E24.filletArc");Q0=makeQuery(id+"F2.boolean.opBoolean","SPLIT",FACE,{"disambiguationData":[TD([makeQuery(id+"F1.opExtrude","SWEPT_FACE",FACE,{"disambiguationData":[OSD([subQ6])]})])],"derivedFrom":makeQuery(id+"F1.opExtrude","CAP_FACE",FACE,{"disambiguationData":[OSD([subQ6,subQ8,subQ9,subQ7,subQ4,subQ3,subQ2,subQ1,subQ0,subQ5,subQ10,subQ11])],"isStart":true})});}
            var sketch = newSketch(context, id + "F16", { "sketchPlane" : qUnion([Q0])});
            skArc(sketch, "E79", {"start": v(14.53, 104.25) * mm, "mid": v(-0.47, 119.25) * mm, "end": v(-15.47, 104.25) * mm});
            skLineSegment(sketch, "E80", {"start": v(-15.47, 104.25) * mm, "end": v(-15.47, 92.25) * mm});
            skLineSegment(sketch, "E81", {"start": v(14.53, 104.25) * mm, "end": v(14.53, 92.25) * mm});
            skLineSegment(sketch, "E82", {"start": v(-15.47, 92.25) * mm, "end": v(-33.47, 74.25) * mm});
            skLineSegment(sketch, "E83", {"start": v(14.53, 92.25) * mm, "end": v(32.53, 74.25) * mm});
            skCircle(sketch, "E84", {"center": v(-0.47, 104.25) * mm, "radius": 6 * mm});
            skLineSegment(sketch, "E85", {"start": v(-0.47, 104.25) * mm, "end": v(-0.47, 74.25) * mm, "construction": true});
            skLineSegment(sketch, "E86", {"start": v(-74.25, 0) * mm, "end": v(74.25, 0) * mm, "construction": true});
            skArc(sketch, "E87.MirrorCS", {"start": v(14.53, -104.25) * mm, "mid": v(-0.47, -119.25) * mm, "end": v(-15.47, -104.25) * mm});
            skCircle(sketch, "E88.MirrorC", {"center": v(-0.47, -104.25) * mm, "radius": 6 * mm});
            skLineSegment(sketch, "E89.MirrorCS", {"start": v(-15.47, -104.25) * mm, "end": v(-15.47, -92.25) * mm});
            skLineSegment(sketch, "E90.MirrorCS", {"start": v(14.53, -104.25) * mm, "end": v(14.53, -92.25) * mm});
            skLineSegment(sketch, "E91.MirrorCS", {"start": v(14.53, -92.25) * mm, "end": v(32.53, -74.25) * mm});
            skLineSegment(sketch, "E92.MirrorCS", {"start": v(-15.47, -92.25) * mm, "end": v(-33.47, -74.25) * mm});
            skLineSegment(sketch, "E93.MirrorCS", {"start": v(-0.47, -104.25) * mm, "end": v(-0.47, -74.25) * mm, "construction": true});
            skSolve(sketch);
        }
        {
            var Q0;
            Q0=makeQuery(id+"F16.imprint","IMPRINT",FACE,{"disambiguationData":[TD([[makeQuery(id+"F16.imprint","IMPRINT",EDGE,{"derivedFrom":sQuery(id+"F16.wireOp",EDGE,"E79")}),1.0]])]});
            var Q1;
            Q1=makeQuery(id+"F16.imprint","IMPRINT",FACE,{"disambiguationData":[TD([[makeQuery(id+"F16.imprint","IMPRINT",EDGE,{"derivedFrom":makeQuery(id+"F1.opExtrude","CAP_EDGE",EDGE,{"disambiguationData":[OSD([sQuery(id+"F0.wireOp",EDGE,"E1.left")])],"isStart":true})}),-1.0]])]});
            var Q2;
            Q2=makeQuery(id+"F16.imprint","IMPRINT",FACE,{"disambiguationData":[TD([[makeQuery(id+"F16.imprint","IMPRINT",EDGE,{"derivedFrom":sQuery(id+"F16.wireOp",EDGE,"E88.MirrorC")}),1.0]])]});
            var Q3;
            Q3=makeQuery(id+"F2.opExtrude","CAP_FACE",FACE,{"disambiguationData":[OSD([sQuery(id+"F0.wireOp",EDGE,"E12"),sQuery(id+"F0.wireOp",EDGE,"E13"),sQuery(id+"F0.wireOp",EDGE,"E14"),sQuery(id+"F0.wireOp",EDGE,"E15"),sQuery(id+"F0.wireOp",EDGE,"E17.filletArc"),sQuery(id+"F0.wireOp",EDGE,"E18.filletArc"),sQuery(id+"F0.wireOp",EDGE,"E19.filletArc"),sQuery(id+"F0.wireOp",EDGE,"E20.filletArc"),sQuery(id+"F0.wireOp",EDGE,"E25.0"),sQuery(id+"F0.wireOp",EDGE,"E25.1"),sQuery(id+"F0.wireOp",EDGE,"E25.2"),sQuery(id+"F0.wireOp",EDGE,"E25.3"),sQuery(id+"F0.wireOp",EDGE,"E25.4"),sQuery(id+"F0.wireOp",EDGE,"E25.5"),sQuery(id+"F0.wireOp",EDGE,"E25.6"),sQuery(id+"F0.wireOp",EDGE,"E25.7")])],"isStart":false});
            extrude(context, id + "F17", {"entities" : qUnion([Q0, Q1, Q2]), "endBound" : BoundingType.UP_TO_SURFACE, "depth" : 11 * mm, "endBoundEntityFace" : qUnion([Q3]), "offsetDistance" : 25 * mm});
        }
    });
